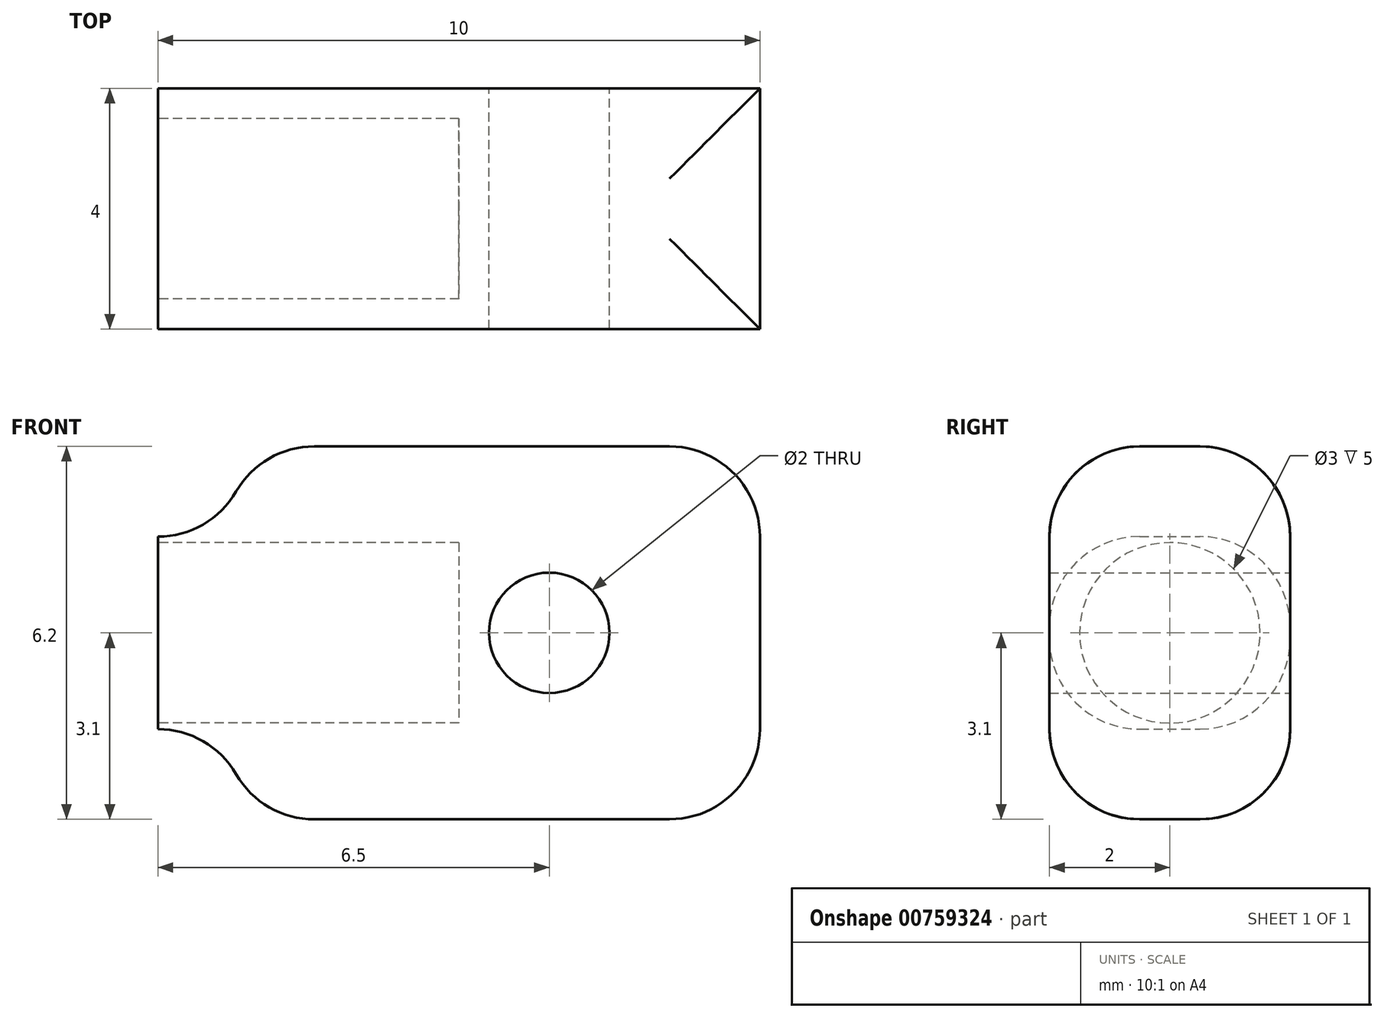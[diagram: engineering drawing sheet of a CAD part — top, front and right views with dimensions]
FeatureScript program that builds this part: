
annotation { "Feature Type Name" : "Feature", "Feature Type Description" : "" }
export const myFeature = defineFeature(function(context is Context, id is Id, definition is map)
    precondition{}
    {
        {
            var Q0;
            Q0=qCreatedBy(makeId("Front.planeOp"),FACE);
            var sketch = newSketch(context, id + "F0", { "sketchPlane" : qUnion([Q0])});
            skLineSegment(sketch, "E0.bottom", {"start": v(-3.5, 3.1) * mm, "end": v(5, 3.1) * mm});
            skLineSegment(sketch, "E0.top", {"start": v(-3.5, -3.1) * mm, "end": v(5, -3.1) * mm});
            skLineSegment(sketch, "E0.left", {"start": v(-5, 1.6) * mm, "end": v(-5, -1.6) * mm});
            skLineSegment(sketch, "E0.right", {"start": v(5, 3.1) * mm, "end": v(5, -3.1) * mm});
            skPoint(sketch, "E0.middle", {"position": v(0, 0) * mm});
            skCircle(sketch, "E1", {"center": v(1.5, 0) * mm, "radius": 1 * mm});
            skArc(sketch, "E2", {"start": v(-3.5, -3.1) * mm, "mid": v(-3.94, -2.04) * mm, "end": v(-5, -1.6) * mm});
            skArc(sketch, "E3", {"start": v(-5, 1.6) * mm, "mid": v(-3.94, 2.04) * mm, "end": v(-3.5, 3.1) * mm});
            skLineSegment(sketch, "E4.bottom", {"start": v(-5, 1.6) * mm, "end": v(0, 1.6) * mm});
            skLineSegment(sketch, "E4.top", {"start": v(-5, -1.6) * mm, "end": v(0, -1.6) * mm});
            skLineSegment(sketch, "E4.right", {"start": v(0, 1.6) * mm, "end": v(0, -1.6) * mm});
            skSolve(sketch);
        }
        {
            var Q0;
            Q0 = qSketchRegion(id + "F0", true);
            extrude(context, id + "F1", {"entities" : qUnion([Q0]), "depth" : 4 * mm, "offsetDistance" : 25 * mm});
        }
        {
            var Q0;
            Q0=makeQuery(id+"F1.opExtrude","SWEPT_EDGE",EDGE,{"disambiguationData":[OSD([sQuery(id+"F0.wireOp",EDGE,"E0.bottom"),sQuery(id+"F0.wireOp",EDGE,"E3")])]});
            var Q1;
            Q1=makeQuery(id+"F1.opExtrude","SWEPT_EDGE",EDGE,{"disambiguationData":[OSD([sQuery(id+"F0.wireOp",EDGE,"E0.top"),sQuery(id+"F0.wireOp",EDGE,"E2")])]});
            fillet(context, id + "F2", {"entities" : qUnion([Q0, Q1]), "radius" : 1.5 * mm, "tangentPropagation" : true, "allowEdgeOverflow" : false});
        }
        {
            var Q0;
            Q0=makeQuery(id+"F1.opExtrude","SWEPT_FACE",FACE,{"disambiguationData":[OSD([sQuery(id+"F0.wireOp",EDGE,"E0.left")])]});
            var sketch = newSketch(context, id + "F3", { "sketchPlane" : qUnion([Q0])});
            skPoint(sketch, "E5.center.orphan", {"position": v(2.74, 0) * mm});
            skCircle(sketch, "E6", {"center": v(2, 0) * mm, "radius": 1.5 * mm});
            skPoint(sketch, "E6.centerSnap0", {"position": v(2, 1.6) * mm});
            skSolve(sketch);
        }
        {
            var Q0;
            Q0 = qSketchRegion(id + "F3", true);
            extrude(context, id + "F4", {"entities" : qUnion([Q0]), "operationType" : NewBodyOperationType.REMOVE, "oppositeDirection" : true, "depth" : 5 * mm, "offsetDistance" : 25 * mm});
        }
        {
            var Q0;
            Q0=makeQuery(id+"F1.opExtrude","SWEPT_EDGE",EDGE,{"disambiguationData":[OSD([sQuery(id+"F0.wireOp",EDGE,"E0.bottom"),sQuery(id+"F0.wireOp",EDGE,"E0.right")])]});
            var Q1;
            Q1=makeQuery(id+"F1.opExtrude","CAP_EDGE",EDGE,{"disambiguationData":[OSD([sQuery(id+"F0.wireOp",EDGE,"E0.bottom")])],"isStart":false});
            var Q2;
            Q2=makeQuery(id+"F1.opExtrude","CAP_EDGE",EDGE,{"disambiguationData":[OSD([sQuery(id+"F0.wireOp",EDGE,"E0.bottom")])],"isStart":true});
            var Q3;
            Q3=makeQuery(id+"F1.opExtrude","SWEPT_EDGE",EDGE,{"disambiguationData":[OSD([sQuery(id+"F0.wireOp",EDGE,"E0.top"),sQuery(id+"F0.wireOp",EDGE,"E0.right")])]});
            var Q4;
            Q4=makeQuery(id+"F1.opExtrude","CAP_EDGE",EDGE,{"disambiguationData":[OSD([sQuery(id+"F0.wireOp",EDGE,"E0.top")])],"isStart":false});
            var Q5;
            Q5=makeQuery(id+"F1.opExtrude","CAP_EDGE",EDGE,{"disambiguationData":[OSD([sQuery(id+"F0.wireOp",EDGE,"E0.top")])],"isStart":true});
            fillet(context, id + "F5", {"entities" : qUnion([Q0, Q1, Q2, Q3, Q4, Q5]), "radius" : 1.5 * mm, "tangentPropagation" : true, "allowEdgeOverflow" : false});
        }
    });
